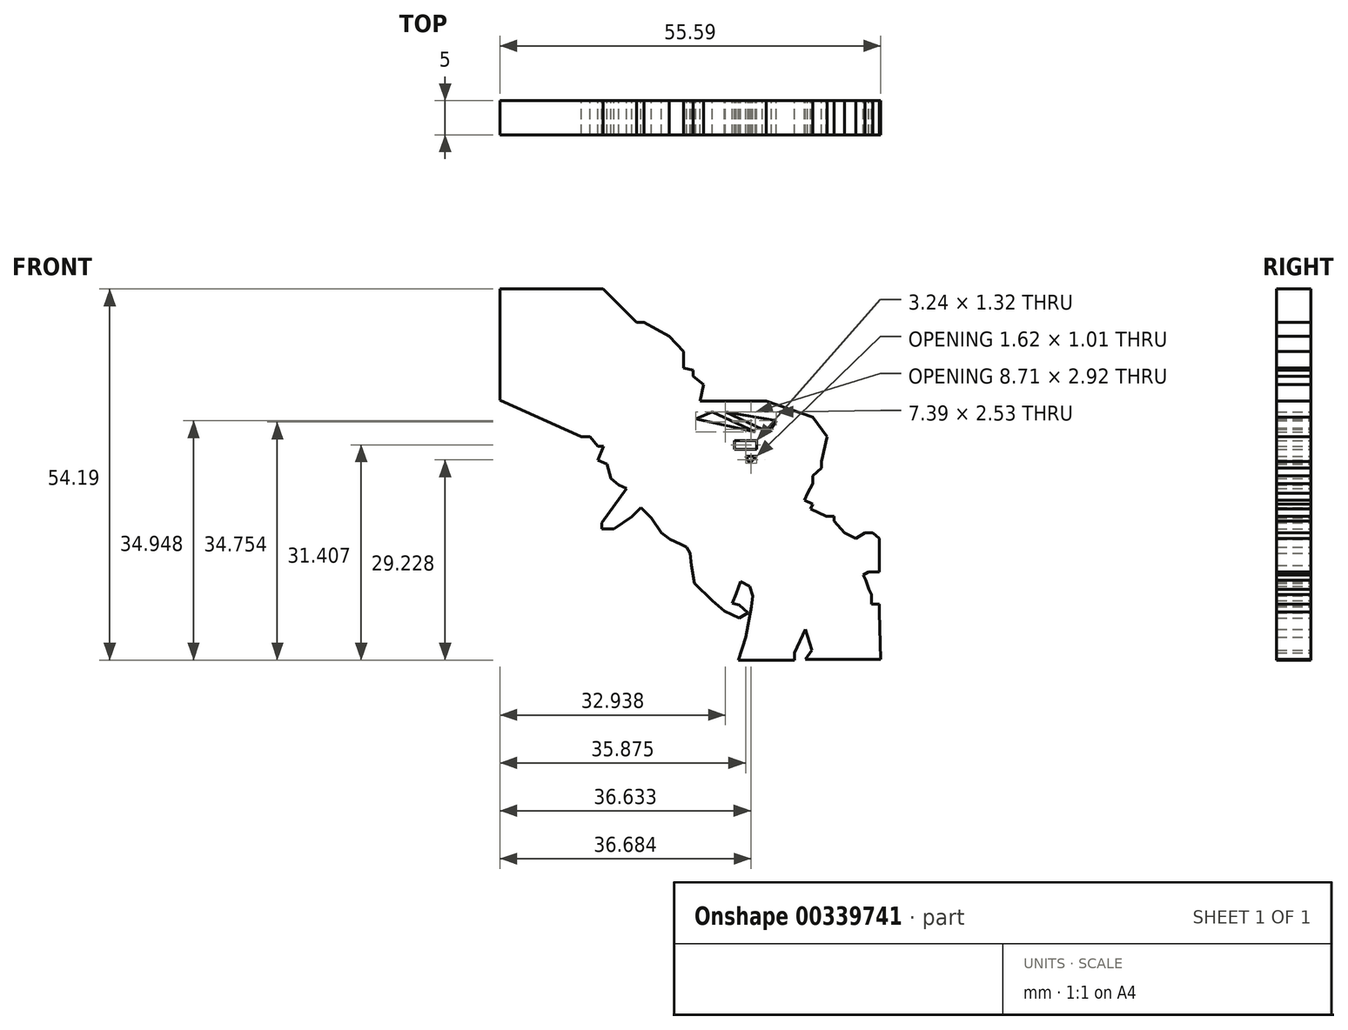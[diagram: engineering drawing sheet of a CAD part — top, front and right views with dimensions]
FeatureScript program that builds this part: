
annotation { "Feature Type Name" : "Feature", "Feature Type Description" : "" }
export const myFeature = defineFeature(function(context is Context, id is Id, definition is map)
    precondition{}
    {
        {
            var Q0;
            Q0=qCreatedBy(makeId("Front.planeOp"),FACE);
            var sketch = newSketch(context, id + "F0", { "sketchPlane" : qUnion([Q0])});
            skLineSegment(sketch, "E0", {"start": v(56.6, 10.74) * mm, "end": v(55.46, 10.74) * mm});
            skLineSegment(sketch, "E1", {"start": v(55.46, 10.74) * mm, "end": v(55.46, 12.14) * mm});
            skLineSegment(sketch, "E2", {"start": v(55.46, 12.14) * mm, "end": v(55.11, 12.93) * mm});
            skLineSegment(sketch, "E3", {"start": v(55.11, 12.93) * mm, "end": v(54.67, 14.24) * mm});
            skLineSegment(sketch, "E4", {"start": v(54.67, 14.24) * mm, "end": v(54.24, 15.03) * mm});
            skLineSegment(sketch, "E5", {"start": v(54.24, 15.03) * mm, "end": v(55.03, 15.47) * mm});
            skLineSegment(sketch, "E6", {"start": v(55.73, 15.47) * mm, "end": v(56.6, 15.47) * mm});
            skLineSegment(sketch, "E7", {"start": v(57.56, 17.48) * mm, "end": v(57.56, 18.27) * mm});
            skLineSegment(sketch, "E8", {"start": v(56.6, 20.38) * mm, "end": v(55.64, 21.16) * mm});
            skLineSegment(sketch, "E9", {"start": v(54.5, 21.16) * mm, "end": v(55.64, 21.16) * mm});
            skLineSegment(sketch, "E10", {"start": v(54.5, 21.16) * mm, "end": v(53.19, 20.38) * mm});
            skLineSegment(sketch, "E11", {"start": v(53.19, 20.38) * mm, "end": v(51.52, 21.16) * mm});
            skLineSegment(sketch, "E12", {"start": v(51.52, 21.16) * mm, "end": v(50.03, 22.92) * mm});
            skLineSegment(sketch, "E13", {"start": v(50.03, 22.92) * mm, "end": v(50.03, 23.62) * mm});
            skLineSegment(sketch, "E14", {"start": v(50.03, 23.62) * mm, "end": v(48.9, 23.62) * mm});
            skLineSegment(sketch, "E15", {"start": v(48.9, 23.62) * mm, "end": v(46.61, 24.67) * mm});
            skLineSegment(sketch, "E16", {"start": v(46.61, 24.67) * mm, "end": v(46.92, 25.34) * mm});
            skLineSegment(sketch, "E17", {"start": v(46.92, 25.34) * mm, "end": v(45.67, 25.92) * mm});
            skLineSegment(sketch, "E18", {"start": v(45.67, 25.92) * mm, "end": v(46.15, 26.95) * mm});
            skLineSegment(sketch, "E19", {"start": v(46.15, 26.95) * mm, "end": v(46.92, 28.35) * mm});
            skLineSegment(sketch, "E20", {"start": v(46.92, 28.35) * mm, "end": v(46.92, 29.49) * mm});
            skLineSegment(sketch, "E21", {"start": v(46.92, 29.49) * mm, "end": v(48.2, 30.63) * mm});
            skLineSegment(sketch, "E22", {"start": v(48.2, 30.63) * mm, "end": v(48.2, 31.6) * mm});
            skLineSegment(sketch, "E23", {"start": v(48.2, 31.6) * mm, "end": v(48.98, 35.18) * mm});
            skLineSegment(sketch, "E24", {"start": v(48.98, 35.18) * mm, "end": v(46.92, 38.08) * mm});
            skLineSegment(sketch, "E25", {"start": v(46.92, 38.08) * mm, "end": v(40.13, 40.44) * mm});
            skLineSegment(sketch, "E26", {"start": v(31.46, 40.44) * mm, "end": v(30.45, 40.44) * mm});
            skLineSegment(sketch, "E27", {"start": v(30.45, 40.44) * mm, "end": v(30.97, 42.8) * mm});
            skLineSegment(sketch, "E28", {"start": v(30.97, 42.8) * mm, "end": v(29.44, 44.03) * mm});
            skLineSegment(sketch, "E29", {"start": v(29.44, 44.03) * mm, "end": v(29.44, 44.9) * mm});
            skLineSegment(sketch, "E30", {"start": v(29.44, 44.9) * mm, "end": v(28.04, 45.22) * mm});
            skLineSegment(sketch, "E31", {"start": v(28.04, 45.22) * mm, "end": v(28.04, 47.63) * mm});
            skLineSegment(sketch, "E32", {"start": v(28.04, 47.63) * mm, "end": v(25.94, 49.9) * mm});
            skLineSegment(sketch, "E33", {"start": v(25.94, 49.9) * mm, "end": v(22.25, 51.92) * mm});
            skLineSegment(sketch, "E34", {"start": v(22.25, 51.92) * mm, "end": v(21.2, 51.92) * mm});
            skLineSegment(sketch, "E35", {"start": v(16.3, 57.56) * mm, "end": v(1.84, 57.56) * mm});
            skLineSegment(sketch, "E36", {"start": v(0, 55.51) * mm, "end": v(0, 54.64) * mm});
            skLineSegment(sketch, "E37", {"start": v(0, 54.64) * mm, "end": v(0, 40.44) * mm});
            skLineSegment(sketch, "E38", {"start": v(13.14, 35.18) * mm, "end": v(14.37, 35.18) * mm});
            skLineSegment(sketch, "E39", {"start": v(14.37, 35.18) * mm, "end": v(15.5, 33.78) * mm});
            skLineSegment(sketch, "E40", {"start": v(15.5, 33.78) * mm, "end": v(16.38, 33.78) * mm});
            skLineSegment(sketch, "E41", {"start": v(16.38, 33.78) * mm, "end": v(15.5, 31.77) * mm});
            skLineSegment(sketch, "E42", {"start": v(15.5, 31.77) * mm, "end": v(16.86, 31.18) * mm});
            skLineSegment(sketch, "E43", {"start": v(16.86, 31.18) * mm, "end": v(17.44, 29.14) * mm});
            skLineSegment(sketch, "E44", {"start": v(17.44, 29.14) * mm, "end": v(18.57, 28.17) * mm});
            skLineSegment(sketch, "E45", {"start": v(18.57, 28.17) * mm, "end": v(19.71, 27.65) * mm});
            skLineSegment(sketch, "E46", {"start": v(19.71, 27.65) * mm, "end": v(16.12, 22.65) * mm});
            skLineSegment(sketch, "E47", {"start": v(16.12, 22.65) * mm, "end": v(16.12, 21.78) * mm});
            skLineSegment(sketch, "E48", {"start": v(16.12, 21.78) * mm, "end": v(17.87, 21.78) * mm});
            skLineSegment(sketch, "E49", {"start": v(17.87, 21.78) * mm, "end": v(20.5, 23.53) * mm});
            skLineSegment(sketch, "E50", {"start": v(20.5, 23.53) * mm, "end": v(21.82, 24.84) * mm});
            skLineSegment(sketch, "E51", {"start": v(21.82, 24.84) * mm, "end": v(23.35, 23.31) * mm});
            skLineSegment(sketch, "E52", {"start": v(23.35, 23.31) * mm, "end": v(24.8, 21.16) * mm});
            skLineSegment(sketch, "E53", {"start": v(24.8, 21.16) * mm, "end": v(26.08, 20.24) * mm});
            skLineSegment(sketch, "E54", {"start": v(26.08, 20.24) * mm, "end": v(27.6, 19.5) * mm});
            skLineSegment(sketch, "E55", {"start": v(27.6, 19.5) * mm, "end": v(28.48, 19.06) * mm});
            skLineSegment(sketch, "E56", {"start": v(28.48, 19.06) * mm, "end": v(29, 18.18) * mm});
            skLineSegment(sketch, "E57", {"start": v(29, 18.18) * mm, "end": v(29.18, 16.43) * mm});
            skLineSegment(sketch, "E58", {"start": v(29.18, 16.43) * mm, "end": v(29.62, 13.8) * mm});
            skLineSegment(sketch, "E59", {"start": v(29.62, 13.8) * mm, "end": v(32.24, 11.26) * mm});
            skLineSegment(sketch, "E60", {"start": v(32.24, 11.26) * mm, "end": v(34, 9.77) * mm});
            skLineSegment(sketch, "E61", {"start": v(34, 9.77) * mm, "end": v(36.19, 8.72) * mm});
            skLineSegment(sketch, "E62", {"start": v(36.19, 8.72) * mm, "end": v(37.41, 9.51) * mm});
            skLineSegment(sketch, "E63", {"start": v(37.41, 9.51) * mm, "end": v(36.19, 10.65) * mm});
            skLineSegment(sketch, "E64", {"start": v(36.19, 10.65) * mm, "end": v(35.14, 10.91) * mm});
            skLineSegment(sketch, "E65", {"start": v(35.14, 10.91) * mm, "end": v(35.75, 12.31) * mm});
            skLineSegment(sketch, "E66", {"start": v(35.75, 12.31) * mm, "end": v(36.36, 14.07) * mm});
            skLineSegment(sketch, "E67", {"start": v(36.36, 14.07) * mm, "end": v(37.68, 13.37) * mm});
            skLineSegment(sketch, "E68", {"start": v(37.68, 13.37) * mm, "end": v(38.11, 11.96) * mm});
            skLineSegment(sketch, "E69", {"start": v(38.11, 11.96) * mm, "end": v(37.94, 10.39) * mm});
            skLineSegment(sketch, "E70", {"start": v(37.94, 10.39) * mm, "end": v(37.15, 5.92) * mm});
            skLineSegment(sketch, "E71", {"start": v(37.15, 5.92) * mm, "end": v(36.01, 2.59) * mm});
            skLineSegment(sketch, "E72", {"start": v(42.4, 0.49) * mm, "end": v(42.58, -0.04) * mm});
            skPoint(sketch, "E73.endSnap0", {"position": v(45.12, 1.54) * mm});
            skLineSegment(sketch, "E74", {"start": v(57.56, 0) * mm, "end": v(57.56, 8.63) * mm});
            skPoint(sketch, "E75.startSnap0", {"position": v(33.86, 36.23) * mm});
            skLineSegment(sketch, "E76", {"start": v(56.6, 10.74) * mm, "end": v(56.6, 9.6) * mm});
            skPoint(sketch, "E77.end.orphan", {"position": v(45.21, 3.2) * mm});
            skLineSegment(sketch, "E78", {"start": v(41.62, 0) * mm, "end": v(42.58, -0.04) * mm});
            skPoint(sketch, "E79.end.orphan", {"position": v(45.04, -0.13) * mm});
            skLineSegment(sketch, "E80", {"start": v(43.99, 0) * mm, "end": v(42.58, -0.04) * mm});
            skLineSegment(sketch, "E81", {"start": v(46.22, 0) * mm, "end": v(57.56, 0) * mm});
            skPoint(sketch, "E82.end.orphan", {"position": v(32.24, 36.59) * mm});
            skLineSegment(sketch, "E83", {"start": v(40.13, 40.44) * mm, "end": v(31.46, 40.44) * mm});
            skPoint(sketch, "E84.orphan", {"position": v(29.44, 40.44) * mm});
            skPoint(sketch, "E85.start.orphan", {"position": v(35.49, 35.88) * mm});
            skPoint(sketch, "E86.start.orphan", {"position": v(35.49, 34.66) * mm});
            skPoint(sketch, "E75.end.orphan", {"position": v(32.24, 35) * mm});
            skPoint(sketch, "E75.start.orphan", {"position": v(33.86, 34.66) * mm});
            skPoint(sketch, "E87.start.orphan", {"position": v(29.44, 36.59) * mm});
            skLineSegment(sketch, "E88", {"start": v(0, 54.64) * mm, "end": v(0, 55.51) * mm});
            skLineSegment(sketch, "E89", {"start": v(0, 40.44) * mm, "end": v(0, 54.64) * mm});
            skPoint(sketch, "E73.end.orphan", {"position": v(46.22, 1.54) * mm});
            skLineSegment(sketch, "E90", {"start": v(36.01, 2.59) * mm, "end": v(44.22, 2.59) * mm});
            skLineSegment(sketch, "E91", {"start": v(44.22, 2.59) * mm, "end": v(44.22, 3.66) * mm});
            skLineSegment(sketch, "E92", {"start": v(44.22, 3.66) * mm, "end": v(45.84, 7.06) * mm});
            skLineSegment(sketch, "E93", {"start": v(45.84, 7.06) * mm, "end": v(46.77, 4) * mm});
            skLineSegment(sketch, "E94", {"start": v(46.77, 4) * mm, "end": v(45.84, 2.7) * mm});
            skLineSegment(sketch, "E95", {"start": v(45.84, 2.7) * mm, "end": v(56.82, 2.7) * mm});
            skLineSegment(sketch, "E96", {"start": v(56.82, 2.7) * mm, "end": v(56.6, 9.6) * mm});
            skLineSegment(sketch, "E97", {"start": v(21.2, 51.92) * mm, "end": v(16.3, 56.78) * mm});
            skLineSegment(sketch, "E98", {"start": v(16.3, 56.78) * mm, "end": v(1.23, 56.78) * mm});
            skLineSegment(sketch, "E99", {"start": v(1.23, 56.78) * mm, "end": v(1.23, 40.52) * mm});
            skLineSegment(sketch, "E100", {"start": v(1.23, 40.52) * mm, "end": v(13.14, 35.18) * mm});
            skLineSegment(sketch, "E101", {"start": v(56.6, 15.47) * mm, "end": v(56.6, 20.38) * mm});
            skLineSegment(sketch, "E102", {"start": v(55.03, 15.47) * mm, "end": v(55.73, 15.47) * mm});
            skLineSegment(sketch, "E103", {"start": v(40.85, 36.47) * mm, "end": v(41.56, 37.59) * mm});
            skLineSegment(sketch, "E104", {"start": v(41.56, 37.59) * mm, "end": v(34.17, 38.8) * mm});
            skLineSegment(sketch, "E105", {"start": v(34.17, 38.8) * mm, "end": v(39.53, 36.27) * mm});
            skLineSegment(sketch, "E106", {"start": v(39.53, 36.27) * mm, "end": v(40.85, 36.47) * mm});
            skLineSegment(sketch, "E107", {"start": v(32.24, 38.8) * mm, "end": v(29.81, 37.8) * mm});
            skLineSegment(sketch, "E108", {"start": v(29.81, 37.8) * mm, "end": v(38.52, 35.88) * mm});
            skLineSegment(sketch, "E109", {"start": v(38.52, 35.88) * mm, "end": v(32.24, 38.8) * mm});
            skLineSegment(sketch, "E110", {"start": v(38.72, 34.65) * mm, "end": v(38.72, 33.34) * mm});
            skLineSegment(sketch, "E111", {"start": v(38.72, 33.34) * mm, "end": v(35.49, 33.34) * mm});
            skLineSegment(sketch, "E112", {"start": v(35.49, 33.34) * mm, "end": v(35.49, 34.66) * mm});
            skLineSegment(sketch, "E113", {"start": v(38.72, 34.65) * mm, "end": v(35.49, 34.66) * mm});
            skLineSegment(sketch, "E114", {"start": v(37.71, 31.31) * mm, "end": v(37.1, 32.32) * mm});
            skPoint(sketch, "E114.endSnap0", {"position": v(37.1, 33.34) * mm});
            skLineSegment(sketch, "E115", {"start": v(37.1, 32.32) * mm, "end": v(38.72, 32.32) * mm});
            skLineSegment(sketch, "E116", {"start": v(38.72, 32.32) * mm, "end": v(37.71, 31.31) * mm});
            skSolve(sketch);
        }
        {
            var Q0;
            Q0=makeQuery(id+"F0.imprint","IMPRINT",FACE,{"disambiguationData":[TD([[makeQuery(id+"F0.imprint","IMPRINT",EDGE,{"derivedFrom":sQuery(id+"F0.wireOp",EDGE,"E0")}),1.0]])]});
            extrude(context, id + "F1", {"entities" : qUnion([Q0]), "depth" : 5 * mm, "offsetDistance" : 25 * mm});
        }
    });
